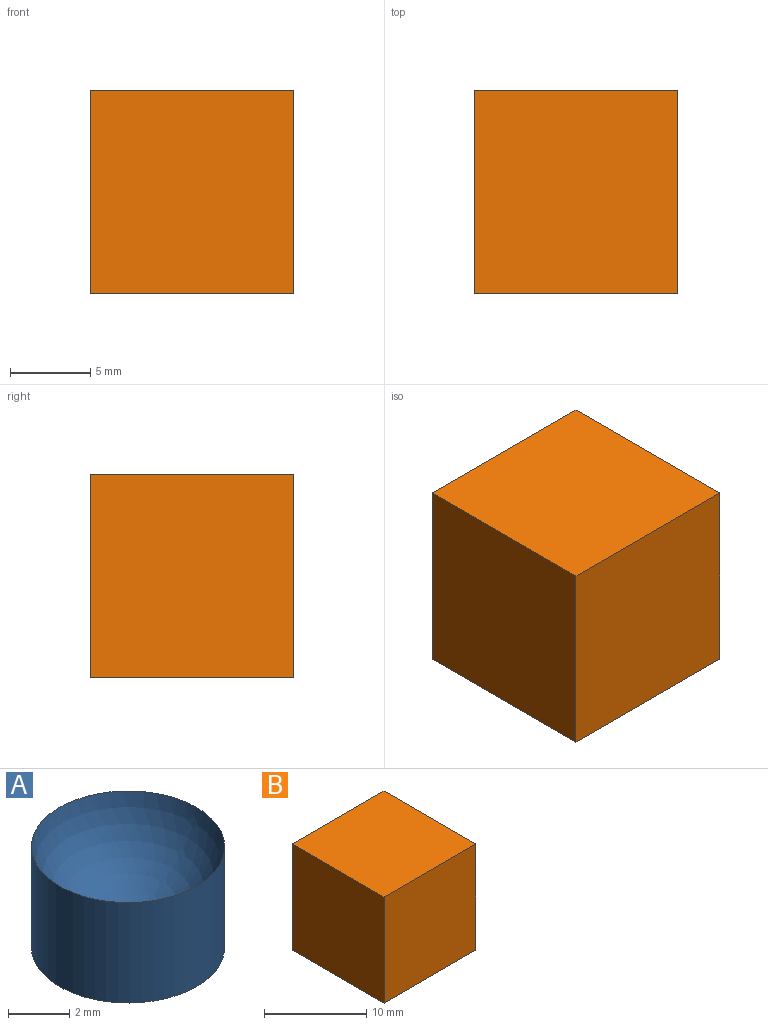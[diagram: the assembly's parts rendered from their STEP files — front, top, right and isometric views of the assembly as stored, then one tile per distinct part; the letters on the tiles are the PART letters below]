
ASSEMBLY  parts=2 mates=1
PART A: 3 faces, bbox 6.3x6.3x4 mm
  f0: cylinder r=3.15mm len=6.3mm, axis (0,0,-1), area 79.2mm2, adj f1,f2
  f1: plane 6.3x6.3mm, normal (0,0,-1), area 31.2mm2, adj f0
  f2: sphere r=3.2mm, area 52.9mm2, adj f0
PART B: 9 faces, bbox 12.7x12.7x12.7 mm
  f0: plane 12.7x12.7mm, normal (-1,0,0), area 161.3mm2, adj f1,f3,f4,f5
  f1: plane 12.7x12.7mm, normal (0,-1,0), area 161.3mm2, adj f0,f2,f4,f5
  f2: plane 12.7x12.7mm, normal (1,0,0), area 161.3mm2, adj f1,f3,f4,f5
  f3: plane 12.7x12.7mm, normal (0,1,0), area 161.3mm2, adj f0,f2,f4,f5
  f4: plane 12.7x12.7mm, normal (0,0,1), area 161.3mm2, adj f0,f1,f2,f3
  f5: plane 12.7x12.7mm, normal (0,0,-1), area 161.3mm2, adj f0,f1,f2,f3
  f6: sphere r=3.2mm, area 64.4mm2, adj f7
  f7: cylinder r=3.2mm len=6.4mm, axis (0,0,-1), area 91.9mm2, adj f6,f8
  f8: plane 6.4x6.4mm, normal (0,0,-1), area 32.2mm2, adj f7
PLACE A rot(axis=(1,0,0),180deg) t=(-5.21,12.93,0.66)mm
PLACE B t=(9.09,2.24,-11.91)mm
MATE slider A.f0 <-> B.f7  axis (0,0,1) through (15.44,8.59,-3.12)mm
